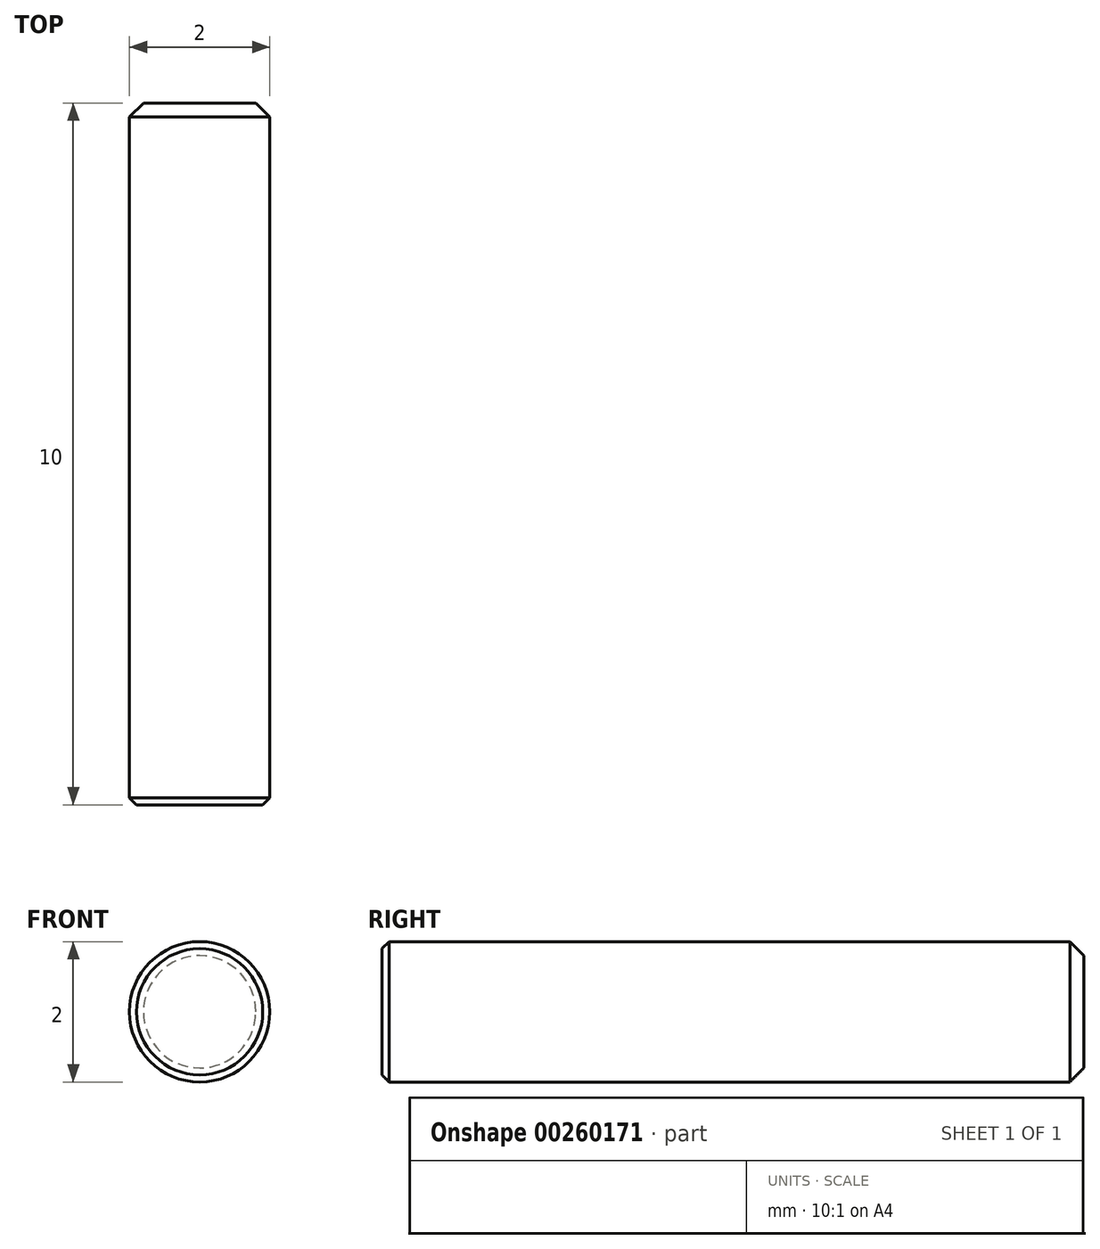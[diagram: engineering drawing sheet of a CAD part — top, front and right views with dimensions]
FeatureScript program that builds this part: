
annotation { "Feature Type Name" : "Feature", "Feature Type Description" : "" }
export const myFeature = defineFeature(function(context is Context, id is Id, definition is map)
    precondition{}
    {
        {
            var Q0;
            Q0=qCreatedBy(makeId("Front.planeOp"),FACE);
            var sketch = newSketch(context, id + "F0", { "sketchPlane" : qUnion([Q0])});
            skCircle(sketch, "E0", {"center": v(0, 0) * mm, "radius": 1 * mm});
            skSolve(sketch);
        }
        {
            var Q0;
            Q0=makeQuery(id+"F0.imprint","IMPRINT",FACE,{"disambiguationData":[TD([[makeQuery(id+"F0.imprint","IMPRINT",EDGE,{"derivedFrom":sQuery(id+"F0.wireOp",EDGE,"E0")}),1.0]])]});
            extrude(context, id + "F1", {"entities" : qUnion([Q0]), "endBound" : BoundingType.SYMMETRIC, "depth" : 10 * mm});
        }
        {
            var Q0;
            Q0=makeQuery(id+"F1.opExtrude","CAP_EDGE",EDGE,{"disambiguationData":[OSD([sQuery(id+"F0.wireOp",EDGE,"E0")])],"isStart":true});
            chamfer(context, id + "F2", {"entities" : qUnion([Q0]), "width" : .2 * mm, "tangentPropagation" : true});
        }
        {
            var Q0;
            Q0=makeQuery(id+"F1.opExtrude","CAP_EDGE",EDGE,{"disambiguationData":[OSD([sQuery(id+"F0.wireOp",EDGE,"E0")])],"isStart":false});
            chamfer(context, id + "F3", {"entities" : qUnion([Q0]), "width" : .1 * mm, "tangentPropagation" : true});
        }
    });
